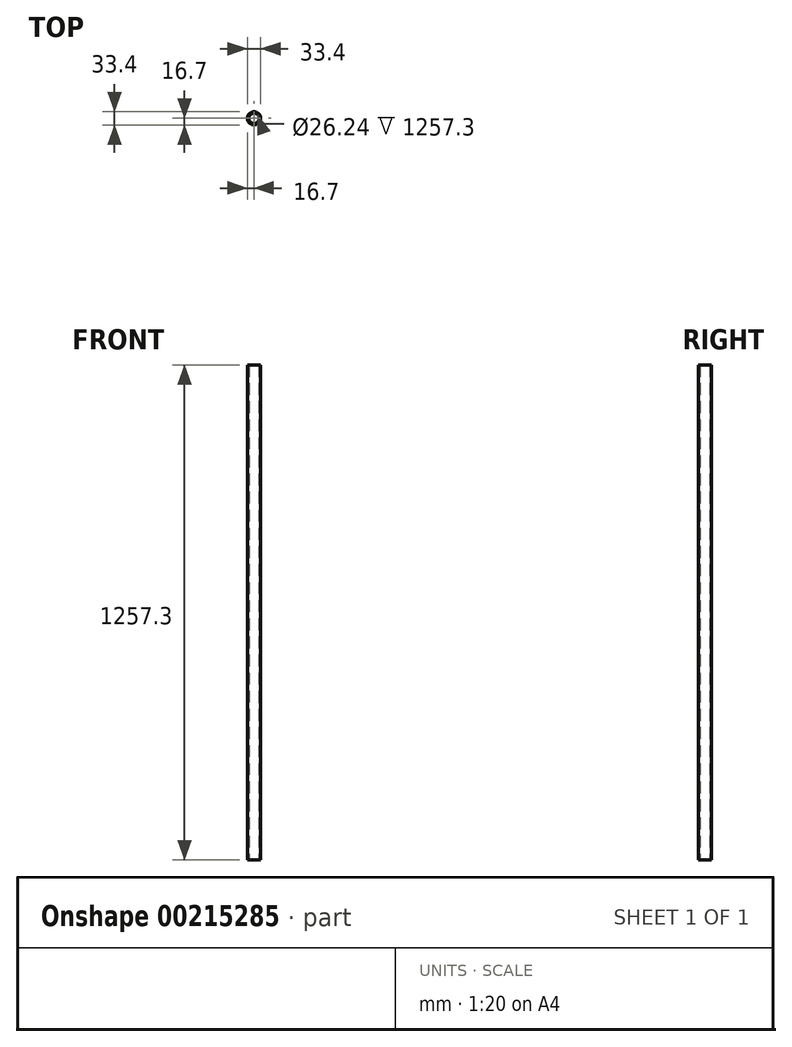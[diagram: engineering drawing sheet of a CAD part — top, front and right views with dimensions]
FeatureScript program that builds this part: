
annotation { "Feature Type Name" : "Feature", "Feature Type Description" : "" }
export const myFeature = defineFeature(function(context is Context, id is Id, definition is map)
    precondition{}
    {
        {
            var Q0;
            Q0=qCreatedBy(makeId("Top.planeOp"),FACE);
            var sketch = newSketch(context, id + "F0", { "sketchPlane" : qUnion([Q0])});
            skCircle(sketch, "E0", {"center": v(0, 0) * mm, "radius": 16.7 * mm});
            skCircle(sketch, "E1", {"center": v(0, 0) * mm, "radius": 13.12 * mm});
            skSolve(sketch);
        }
        {
            var Q0;
            Q0=makeQuery(id+"F0.imprint","IMPRINT",FACE,{"disambiguationData":[TD([[makeQuery(id+"F0.imprint","IMPRINT",EDGE,{"derivedFrom":sQuery(id+"F0.wireOp",EDGE,"E0")}),1.0]])]});
            extrude(context, id + "F1", {"entities" : qUnion([Q0]), "depth" : 1257.3 * mm});
        }
    });
